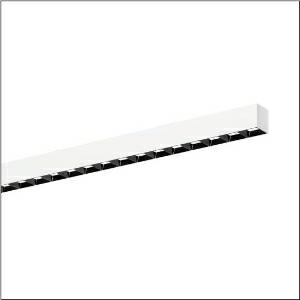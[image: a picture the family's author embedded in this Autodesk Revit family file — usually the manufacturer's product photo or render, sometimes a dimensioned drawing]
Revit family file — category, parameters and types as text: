
# Revit family: silica_r__21_51mx21tat4w_a490
name_source: partatom
category: Lighting Fixtures
units: mm (PartAtom-declared; Revit-internal decimal feet)

## family parameters
Cut with Voids When Loaded = No
Host = Face
Light Source = No
Part Type = Normal
Room Calculation Point = No
Round Connector Dimension = Use Diameter
Shared = No

## types (1)
- --- (1 x LED, 3720 lm, 32.2 W, 6500K)
    Apparent Load = 32 VA
    CIE Flux Codes = 85 99 100 100 100
    Color Rendering = 80
    Color Temperature = 6500K
    Default Elevation = 1800 mm
    Description = Silica® 21, office luminaire, primary light control with darklight reflector, of PMMA, black, CAT 2 (L<= 3000cd/m²), light emission: direct distribution, primary light characteristic: symmetric, installation type: surface-mounted, LED, rated luminous flux: 3.720lm, luminous efficacy: 110lm/W, light colour: 8tw, colour temperature: 2700..6500K, control gear: DALI DT8, with terminal, 3+2-pole, max. 2.5mm², mains connection: 220..240V, AC, 50/60Hz, rated input power: 33.8W, luminaire housing, of aluminium, traffic white (RAL 9016), length: 1.204mm, width: 53mm, height: 53mm, protection rating (complete): IP20, insulation class (complete): insulation class I (protective earthing), certification: CE, permissible operating ambient temperature: 0..+35°C, standard: EN 50419, packaging unit: 1 piece
    Height = 53 mm
    Lamp = 1 x LED
    Lamp Light Flux = 3720 lm
    Lamp Power = 32.2 W
    Lamp count = 1
    Length = 1204 mm
    Luminous efficacy = 116 lm/W
    Manufacturer = Siteco
    ModVariant = No
    Model = 51MX21TAT4W
    Mounting Place = Ceiling
    Mounting Type = Surface mounted
    Number of Poles = 1
    OnlyDefault = Yes
    Power Factor = 1
    Product Name = Silica® 21
    Product group = office luminaire | ceiling mounted
    ProductGroupID = 302
    Protection Class = Protection class I
    Protection Degree = IP 20
    RLX_Detail_Level = 1
    RLX_Emergency_Light_Flux = 0 lm
    RLX_Emergency_Type = 0
    RLX_Emergency_Type_DB = No
    RlxData = <blob elided: 37917 chars, md5=95598518>
    Socket = socket
    Standby Power = 0 W
    System Light Flux = 3720 lm
    System Power = 32 W
    Type Comments = individual setting
    Type Image = l_1335873.jpg
    URL = http://relux.com
    VarID = @adj_140088
    Voltage = 0 V
    Weight = 0.00 kg
    Width = 53 mm

## geometry (parser evidence)
native form markers: Blend x4, Sweep x10
no freeform markers — native parametric forms only
